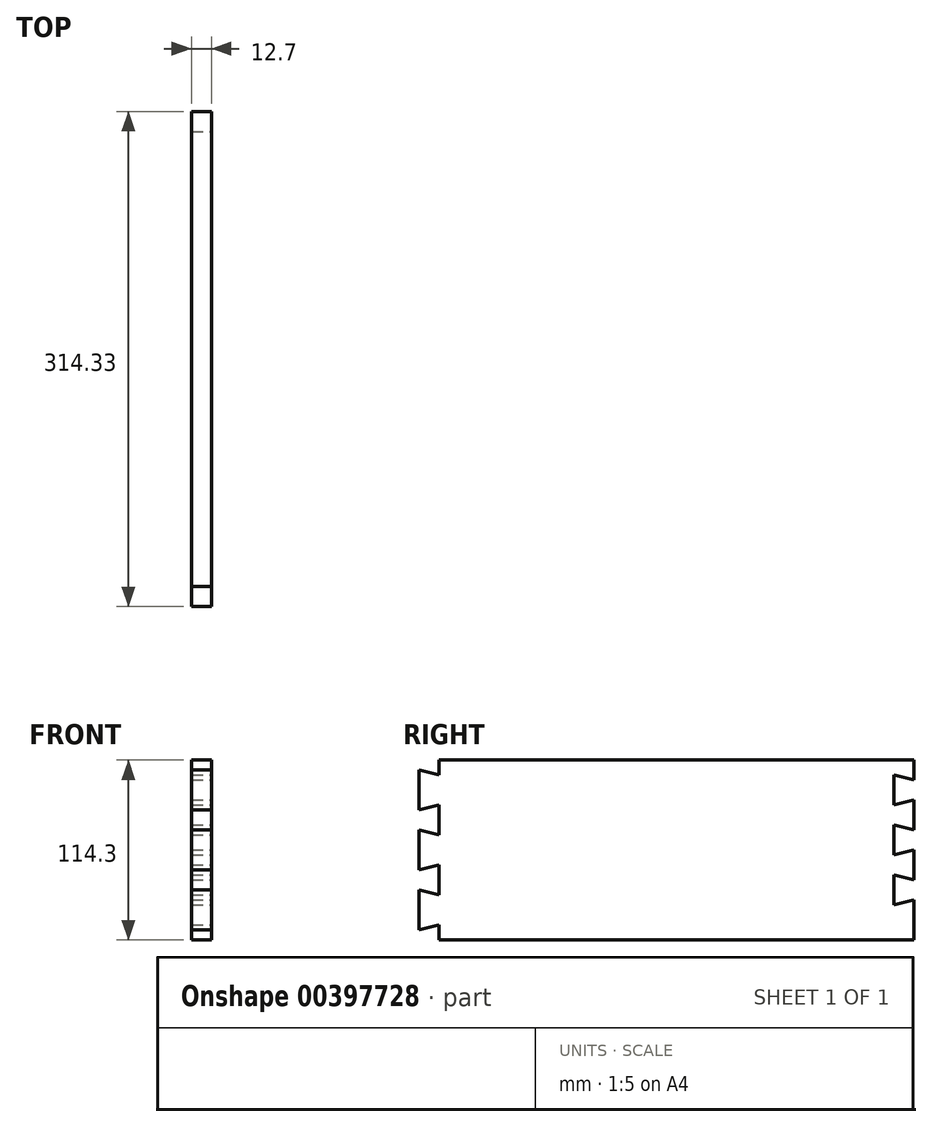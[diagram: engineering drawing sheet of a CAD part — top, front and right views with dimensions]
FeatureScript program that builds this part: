
annotation { "Feature Type Name" : "Feature", "Feature Type Description" : "" }
export const myFeature = defineFeature(function(context is Context, id is Id, definition is map)
    precondition{}
    {
        {
            var Q0;
            Q0=qCreatedBy(makeId("Right.planeOp"),FACE);
            var sketch = newSketch(context, id + "F0", { "sketchPlane" : qUnion([Q0])});
            skLineSegment(sketch, "E0.bottom", {"start": v(0, 0) * mm, "end": v(314.32, 0) * mm});
            skLineSegment(sketch, "E0.top", {"start": v(0, 114.3) * mm, "end": v(314.33, 114.3) * mm});
            skLineSegment(sketch, "E0.left", {"start": v(0, 0) * mm, "end": v(0, 114.3) * mm});
            skLineSegment(sketch, "E0.right", {"start": v(314.33, 0) * mm, "end": v(314.33, 114.3) * mm});
            skSolve(sketch);
        }
        {
            var Q0;
            Q0=makeQuery(id+"F0.imprint","IMPRINT",FACE,{"disambiguationData":[TD([[makeQuery(id+"F0.imprint","IMPRINT",EDGE,{"derivedFrom":sQuery(id+"F0.wireOp",EDGE,"E0.bottom")}),1.0]])]});
            extrude(context, id + "F1", {"entities" : qUnion([Q0]), "depth" : 12.7 * mm});
        }
        {
            var Q0;
            Q0=makeQuery(id+"F1.opExtrude","CAP_FACE",FACE,{"disambiguationData":[OSD([sQuery(id+"F0.wireOp",EDGE,"E0.bottom"),sQuery(id+"F0.wireOp",EDGE,"E0.top"),sQuery(id+"F0.wireOp",EDGE,"E0.left"),sQuery(id+"F0.wireOp",EDGE,"E0.right")])],"isStart":false});
            var sketch = newSketch(context, id + "F2", { "sketchPlane" : qUnion([Q0])});
            skLineSegment(sketch, "E1", {"start": v(12.7, 114.3) * mm, "end": v(12.7, 104.78) * mm});
            skLineSegment(sketch, "E2", {"start": v(12.7, 114.3) * mm, "end": v(0, 114.3) * mm});
            skLineSegment(sketch, "E3", {"start": v(0, 114.3) * mm, "end": v(0, 107.94) * mm});
            skLineSegment(sketch, "E4", {"start": v(0, 107.94) * mm, "end": v(12.7, 104.78) * mm});
            skLineSegment(sketch, "E5", {"start": v(12.7, 66.67) * mm, "end": v(0, 69.84) * mm});
            skLineSegment(sketch, "E6", {"start": v(0, 82.56) * mm, "end": v(0, 69.84) * mm});
            skLineSegment(sketch, "E7", {"start": v(0, 82.56) * mm, "end": v(12.7, 85.72) * mm});
            skLineSegment(sketch, "E8", {"start": v(12.7, 47.63) * mm, "end": v(0, 44.46) * mm});
            skLineSegment(sketch, "E9.trimOffspring", {"start": v(12.7, 85.72) * mm, "end": v(12.7, 66.67) * mm});
            skLineSegment(sketch, "E10", {"start": v(12.7, 66.67) * mm, "end": v(12.7, 104.78) * mm, "construction": true});
            skLineSegment(sketch, "E11.trimOffspring", {"start": v(12.7, 47.63) * mm, "end": v(12.7, 28.58) * mm});
            skLineSegment(sketch, "E12", {"start": v(12.7, 47.63) * mm, "end": v(12.7, 85.72) * mm, "construction": true});
            skPoint(sketch, "E13", {"position": v(12.7, 76.2) * mm});
            skLineSegment(sketch, "E14", {"start": v(0, 44.46) * mm, "end": v(0, 31.74) * mm});
            skLineSegment(sketch, "E15", {"start": v(0, 31.74) * mm, "end": v(12.7, 28.58) * mm});
            skLineSegment(sketch, "E16", {"start": v(12.7, 28.58) * mm, "end": v(12.7, 47.63) * mm});
            skPoint(sketch, "E17", {"position": v(12.7, 38.1) * mm});
            skLineSegment(sketch, "E18", {"start": v(12.7, 9.52) * mm, "end": v(0, 6.36) * mm});
            skLineSegment(sketch, "E19", {"start": v(0, 6.36) * mm, "end": v(0, 0) * mm});
            skLineSegment(sketch, "E20", {"start": v(0, 0) * mm, "end": v(12.7, 0) * mm});
            skLineSegment(sketch, "E21.trimOffspring", {"start": v(12.7, 9.52) * mm, "end": v(12.7, 0) * mm});
            skLineSegment(sketch, "E22", {"start": v(12.7, 28.58) * mm, "end": v(12.7, 9.52) * mm, "construction": true});
            skLineSegment(sketch, "E23", {"start": v(12.7, 0) * mm, "end": v(0, 0) * mm});
            skLineSegment(sketch, "E24", {"start": v(314.33, 101.6) * mm, "end": v(301.62, 104.77) * mm});
            skLineSegment(sketch, "E25", {"start": v(301.62, 104.77) * mm, "end": v(301.62, 85.73) * mm});
            skLineSegment(sketch, "E26", {"start": v(301.62, 85.73) * mm, "end": v(314.33, 88.9) * mm});
            skLineSegment(sketch, "E27", {"start": v(314.33, 88.9) * mm, "end": v(314.33, 101.6) * mm});
            skLineSegment(sketch, "E28", {"start": v(301.63, 73.02) * mm, "end": v(314.33, 69.85) * mm});
            skLineSegment(sketch, "E29", {"start": v(314.33, 69.85) * mm, "end": v(314.33, 57.15) * mm});
            skLineSegment(sketch, "E30", {"start": v(314.33, 57.15) * mm, "end": v(301.63, 53.98) * mm});
            skLineSegment(sketch, "E31", {"start": v(301.63, 53.98) * mm, "end": v(301.63, 73.02) * mm});
            skLineSegment(sketch, "E32", {"start": v(301.63, 85.73) * mm, "end": v(301.63, 73.02) * mm, "construction": true});
            skLineSegment(sketch, "E33", {"start": v(301.62, 104.77) * mm, "end": v(301.62, 114.3) * mm, "construction": true});
            skLineSegment(sketch, "E34", {"start": v(301.62, 111.13) * mm, "end": v(314.33, 111.13) * mm, "construction": true});
            skPoint(sketch, "E35", {"position": v(301.63, 79.38) * mm});
            skLineSegment(sketch, "E36", {"start": v(301.63, 53.98) * mm, "end": v(301.63, 41.27) * mm, "construction": true});
            skLineSegment(sketch, "E37", {"start": v(301.63, 41.27) * mm, "end": v(314.33, 38.1) * mm});
            skPoint(sketch, "E38", {"position": v(301.63, 47.63) * mm});
            skLineSegment(sketch, "E39", {"start": v(301.63, 41.27) * mm, "end": v(301.63, 22.23) * mm});
            skLineSegment(sketch, "E40", {"start": v(301.63, 22.23) * mm, "end": v(314.33, 25.4) * mm});
            skLineSegment(sketch, "E41", {"start": v(301.63, 22.23) * mm, "end": v(301.63, 0) * mm, "construction": true});
            skLineSegment(sketch, "E42", {"start": v(301.63, 15.88) * mm, "end": v(314.33, 15.88) * mm, "construction": true});
            skSolve(sketch);
        }
        {
            var Q0;
            Q0=makeQuery(id+"F2.imprint","IMPRINT",FACE,{"disambiguationData":[TD([[makeQuery(id+"F2.imprint","IMPRINT",EDGE,{"derivedFrom":sQuery(id+"F2.wireOp",EDGE,"E18")}),1.0]])]});
            var Q1;
            Q1=makeQuery(id+"F2.imprint","IMPRINT",FACE,{"disambiguationData":[TD([[makeQuery(id+"F2.imprint","IMPRINT",EDGE,{"derivedFrom":sQuery(id+"F2.wireOp",EDGE,"E8")}),1.0]])]});
            var Q2;
            Q2=makeQuery(id+"F2.imprint","IMPRINT",FACE,{"disambiguationData":[TD([[makeQuery(id+"F2.imprint","IMPRINT",EDGE,{"derivedFrom":sQuery(id+"F2.wireOp",EDGE,"E5")}),-1.0]])]});
            var Q3;
            Q3=makeQuery(id+"F2.imprint","IMPRINT",FACE,{"disambiguationData":[TD([[makeQuery(id+"F2.imprint","IMPRINT",EDGE,{"derivedFrom":sQuery(id+"F2.wireOp",EDGE,"E1")}),-1.0]])]});
            var Q4;
            Q4=makeQuery(id+"F2.imprint","IMPRINT",FACE,{"disambiguationData":[TD([[makeQuery(id+"F2.imprint","IMPRINT",EDGE,{"derivedFrom":sQuery(id+"F2.wireOp",EDGE,"E24")}),1.0]])]});
            var Q5;
            Q5=makeQuery(id+"F2.imprint","IMPRINT",FACE,{"disambiguationData":[TD([[makeQuery(id+"F2.imprint","IMPRINT",EDGE,{"derivedFrom":sQuery(id+"F2.wireOp",EDGE,"E28")}),-1.0]])]});
            var Q6;
            {var subQ0=sQuery(id+"F2.wireOp",EDGE,"E37");Q6=makeQuery(id+"F2.imprint","IMPRINT",FACE,{"disambiguationData":[TD([[makeQuery(id+"F2.imprint","IMPRINT",EDGE,{"derivedFrom":subQ0}),-1.0]])]});}
            extrude(context, id + "F3", {"entities" : qUnion([Q0, Q1, Q2, Q3, Q4, Q5, Q6]), "operationType" : NewBodyOperationType.REMOVE, "endBound" : BoundingType.THROUGH_ALL, "oppositeDirection" : true, "depth" : 25.4 * mm});
        }
    });
